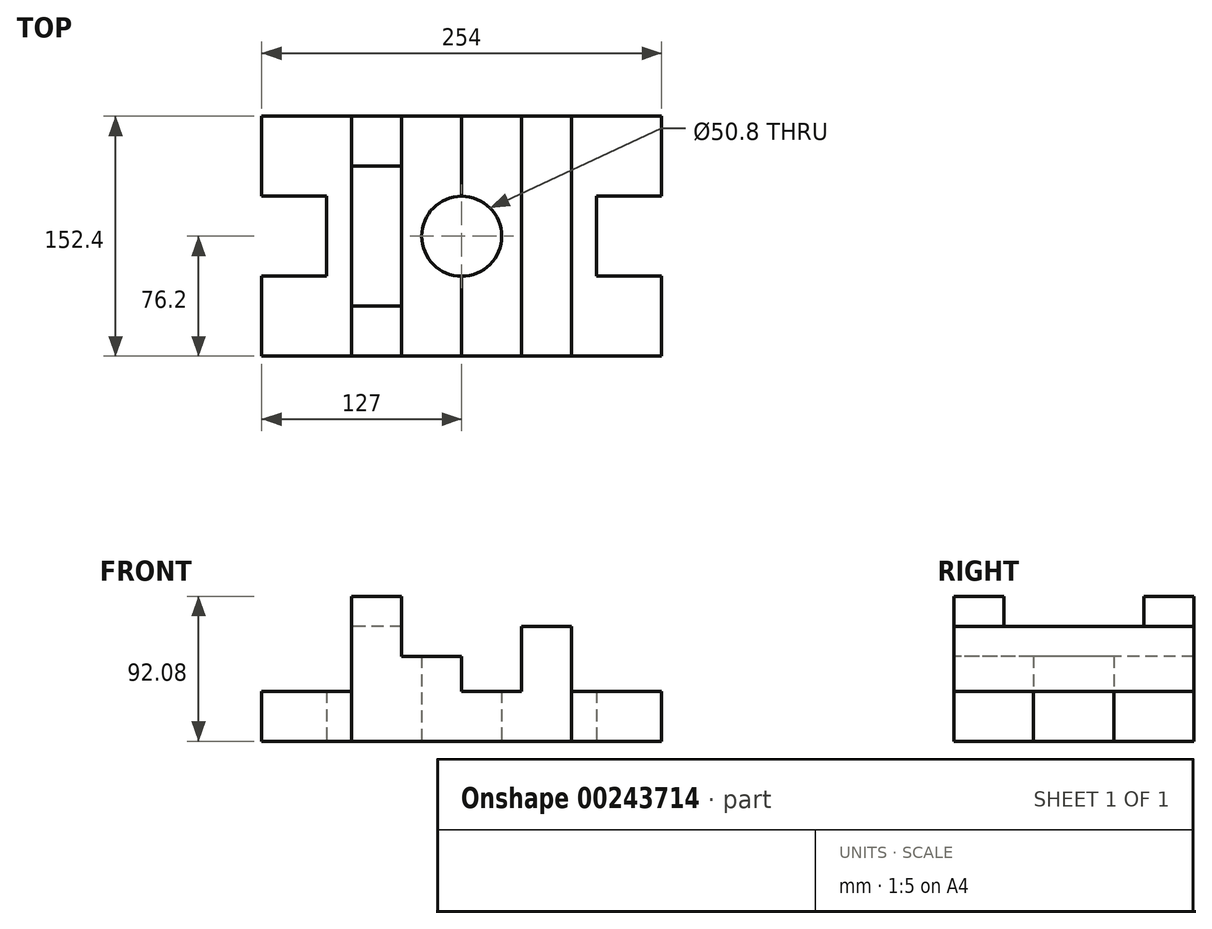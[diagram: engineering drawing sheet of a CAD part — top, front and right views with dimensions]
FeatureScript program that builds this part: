
annotation { "Feature Type Name" : "Feature", "Feature Type Description" : "" }
export const myFeature = defineFeature(function(context is Context, id is Id, definition is map)
    precondition{}
    {
        {
            var Q0;
            Q0=qCreatedBy(makeId("Top.planeOp"),FACE);
            var sketch = newSketch(context, id + "F0", { "sketchPlane" : qUnion([Q0])});
            skLineSegment(sketch, "E0", {"start": v(0, 76.2) * mm, "end": v(-127, 76.2) * mm});
            skLineSegment(sketch, "E1", {"start": v(-127, 76.2) * mm, "end": v(-127, 25.4) * mm});
            skLineSegment(sketch, "E2", {"start": v(0, -76.2) * mm, "end": v(-127, -76.2) * mm});
            skLineSegment(sketch, "E3", {"start": v(-127, 25.4) * mm, "end": v(-85.72, 25.4) * mm});
            skLineSegment(sketch, "E4", {"start": v(-127, -25.4) * mm, "end": v(-85.72, -25.4) * mm});
            skLineSegment(sketch, "E5", {"start": v(-85.72, 25.4) * mm, "end": v(-85.72, -25.4) * mm});
            skLineSegment(sketch, "E6", {"start": v(0, 76.2) * mm, "end": v(0, -76.2) * mm});
            skLineSegment(sketch, "E7.trimOffspring", {"start": v(-127, -25.4) * mm, "end": v(-127, -76.2) * mm});
            skLineSegment(sketch, "E8.MirrorCS", {"start": v(0, 76.2) * mm, "end": v(127, 76.2) * mm});
            skLineSegment(sketch, "E9.MirrorCS", {"start": v(127, 76.2) * mm, "end": v(127, 25.4) * mm});
            skLineSegment(sketch, "E10.MirrorCS", {"start": v(85.72, 25.4) * mm, "end": v(85.72, -25.4) * mm});
            skLineSegment(sketch, "E11.MirrorCS", {"start": v(127, 25.4) * mm, "end": v(85.72, 25.4) * mm});
            skLineSegment(sketch, "E12.MirrorCS", {"start": v(127, -25.4) * mm, "end": v(85.72, -25.4) * mm});
            skLineSegment(sketch, "E13.MirrorCS", {"start": v(127, -25.4) * mm, "end": v(127, -76.2) * mm});
            skLineSegment(sketch, "E14.MirrorCS", {"start": v(0, -76.2) * mm, "end": v(127, -76.2) * mm});
            skLineSegment(sketch, "E15", {"start": v(127, 76.2) * mm, "end": v(69.85, 76.2) * mm});
            skLineSegment(sketch, "E16", {"start": v(69.85, 76.2) * mm, "end": v(38.1, 76.2) * mm});
            skLineSegment(sketch, "E17", {"start": v(38.1, 76.2) * mm, "end": v(0, 76.2) * mm});
            skLineSegment(sketch, "E18", {"start": v(0, 76.2) * mm, "end": v(38.1, 76.2) * mm});
            skLineSegment(sketch, "E19", {"start": v(38.1, 76.2) * mm, "end": v(38.1, -76.2) * mm});
            skLineSegment(sketch, "E20", {"start": v(69.85, 76.2) * mm, "end": v(69.85, -76.2) * mm});
            skLineSegment(sketch, "E21.MirrorCS", {"start": v(-38.1, 76.2) * mm, "end": v(-38.1, -76.2) * mm});
            skLineSegment(sketch, "E22.MirrorCS", {"start": v(-69.85, 76.2) * mm, "end": v(-69.85, -76.2) * mm});
            skLineSegment(sketch, "E23", {"start": v(38.1, 76.2) * mm, "end": v(38.1, 44.45) * mm});
            skLineSegment(sketch, "E24", {"start": v(38.1, 44.45) * mm, "end": v(69.85, 44.45) * mm});
            skLineSegment(sketch, "E25", {"start": v(38.1, -76.2) * mm, "end": v(38.1, -44.45) * mm});
            skLineSegment(sketch, "E26", {"start": v(38.1, -44.45) * mm, "end": v(69.85, -44.45) * mm});
            skLineSegment(sketch, "E27.MirrorCS", {"start": v(-38.1, 44.45) * mm, "end": v(-69.85, 44.45) * mm});
            skLineSegment(sketch, "E28.MirrorCS", {"start": v(-38.1, -44.45) * mm, "end": v(-69.85, -44.45) * mm});
            skCircle(sketch, "E29", {"center": v(0, 0) * mm, "radius": 25.4 * mm});
            skSolve(sketch);
        }
        {
            var Q0;
            {var subQ5=sQuery(id+"F0.wireOp",EDGE,"E27.MirrorCS");Q0=makeQuery(id+"F0.imprint","IMPRINT",FACE,{"disambiguationData":[TD([[makeQuery(id+"F0.imprint","IMPRINT",EDGE,{"derivedFrom":subQ5}),-1.0]])]});}
            var Q1;
            {var subQ5=sQuery(id+"F0.wireOp",EDGE,"E28.MirrorCS");Q1=makeQuery(id+"F0.imprint","IMPRINT",FACE,{"disambiguationData":[TD([[makeQuery(id+"F0.imprint","IMPRINT",EDGE,{"derivedFrom":subQ5}),1.0]])]});}
            var Q2;
            {var subQ3=sQuery(id+"F0.wireOp",EDGE,"E25");Q2=makeQuery(id+"F0.imprint","IMPRINT",FACE,{"disambiguationData":[TD([[makeQuery(id+"F0.imprint","IMPRINT",EDGE,{"derivedFrom":subQ3}),-1.0]])]});}
            var Q3;
            {var subQ0=sQuery(id+"F0.wireOp",EDGE,"E16");Q3=makeQuery(id+"F0.imprint","IMPRINT",FACE,{"disambiguationData":[TD([[makeQuery(id+"F0.imprint","IMPRINT",EDGE,{"derivedFrom":subQ0}),1.0]])]});}
            extrude(context, id + "F1", {"entities" : qUnion([Q0, Q1, Q2, Q3]), "depth" : 92.07 * mm});
        }
        {
            var Q0;
            {var subQ0=sQuery(id+"F0.wireOp",EDGE,"E27.MirrorCS");Q0=makeQuery(id+"F0.imprint","IMPRINT",FACE,{"disambiguationData":[TD([[makeQuery(id+"F0.imprint","IMPRINT",EDGE,{"derivedFrom":subQ0}),1.0]])]});}
            var Q1;
            Q1=makeQuery(id+"F0.imprint","IMPRINT",FACE,{"disambiguationData":[TD([[makeQuery(id+"F0.imprint","IMPRINT",EDGE,{"derivedFrom":sQuery(id+"F0.wireOp",EDGE,"E19")}),1.0]])]});
            extrude(context, id + "F2", {"entities" : qUnion([Q0, Q1]), "depth" : 73.02 * mm});
        }
        {
            var Q0;
            {var subQ5=sQuery(id+"F0.wireOp",EDGE,"E0");var subQ8=sQuery(id+"F0.wireOp",EDGE,"E21.MirrorCS");var subQ12=makeQuery(id+"F0.imprint","INTERSECT",VERTEX,{"derivedFrom":[subQ5,subQ8]});Q0=makeQuery(id+"F0.imprint","IMPRINT",FACE,{"disambiguationData":[TD([[makeQuery(id+"F0.imprint","IMPRINT",EDGE,{"disambiguationData":[TD([[subQ12,-1.0]])],"derivedFrom":subQ8}),1.0]])]});}
            var Q1;
            {var subQ6=sQuery(id+"F0.wireOp",EDGE,"E18");Q1=makeQuery(id+"F0.imprint","IMPRINT",FACE,{"disambiguationData":[TD([[makeQuery(id+"F0.imprint","IMPRINT",EDGE,{"derivedFrom":subQ6}),-1.0]])]});}
            extrude(context, id + "F3", {"entities" : qUnion([Q0, Q1]), "depth" : 53.97 * mm});
        }
        {
            var Q0;
            {var subQ0=sQuery(id+"F0.wireOp",EDGE,"E29");var subQ1=sQuery(id+"F0.wireOp",EDGE,"E6");var subQ2=makeQuery(id+"F0.imprint","INTERSECT",VERTEX,{"disambiguationData":[OD(0.0)],"derivedFrom":[subQ1,subQ0]});Q0=makeQuery(id+"F0.imprint","IMPRINT",FACE,{"disambiguationData":[TD([[makeQuery(id+"F0.imprint","IMPRINT",EDGE,{"disambiguationData":[TD([[subQ2,-1.0]])],"derivedFrom":subQ1}),-1.0]])]});}
            var Q1;
            {var subQ0=sQuery(id+"F0.wireOp",EDGE,"E29");var subQ1=sQuery(id+"F0.wireOp",EDGE,"E6");var subQ2=makeQuery(id+"F0.imprint","INTERSECT",VERTEX,{"disambiguationData":[OD(0.0)],"derivedFrom":[subQ1,subQ0]});Q1=makeQuery(id+"F0.imprint","IMPRINT",FACE,{"disambiguationData":[TD([[makeQuery(id+"F0.imprint","IMPRINT",EDGE,{"disambiguationData":[TD([[subQ2,-1.0]])],"derivedFrom":subQ1}),1.0]])]});}
            extrude(context, id + "F4", {"entities" : qUnion([Q0, Q1]), "operationType" : NewBodyOperationType.ADD, "depth" : 31.75 * mm});
        }
        {
            var Q0;
            Q0=makeQuery(id+"F0.imprint","IMPRINT",FACE,{"disambiguationData":[TD([[makeQuery(id+"F0.imprint","IMPRINT",EDGE,{"derivedFrom":sQuery(id+"F0.wireOp",EDGE,"E9.MirrorCS")}),-1.0]])]});
            var Q1;
            {var subQ4=sQuery(id+"F0.wireOp",EDGE,"E1");Q1=makeQuery(id+"F0.imprint","IMPRINT",FACE,{"disambiguationData":[TD([[makeQuery(id+"F0.imprint","IMPRINT",EDGE,{"derivedFrom":subQ4}),1.0]])]});}
            extrude(context, id + "F5", {"entities" : qUnion([Q0, Q1]), "depth" : 31.75 * mm});
        }
    });
